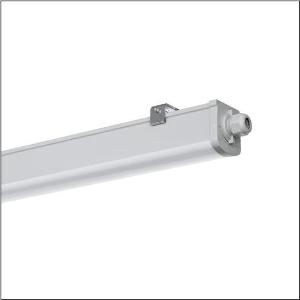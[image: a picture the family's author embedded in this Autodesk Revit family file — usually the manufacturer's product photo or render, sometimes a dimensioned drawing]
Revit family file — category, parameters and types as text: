
# Revit family: monsun_r__31_51fa207d420b_180d
name_source: partatom
category: Lighting Fixtures
units: mm (PartAtom-declared; Revit-internal decimal feet)

## family parameters
Cut with Voids When Loaded = No
Host = Face
Light Source = No
Part Type = Normal
Room Calculation Point = No
Round Connector Dimension = Use Diameter
Shared = No

## types (1)
- Monsun® 31 (1 x LED, 2300 lm, 19 W, 4000K)
    Apparent Load = 19 VA
    CIE Flux Codes = 42 72 91 92 100
    Color Rendering = 80
    Color Temperature = 4000K
    Default Elevation = 1800 mm
    Description = Monsun® 31, damp-proof luminaire, primary optical cover: diffuser, of PC, frosted, light emission: direct distribution, primary light characteristic: symmetric, installation type: surface-mounted, LED, rated luminous flux: 2.300lm, luminous efficacy: 121lm/W, light colour: 840, colour temperature: 4000K, control gear: ECG, with terminal, 3+1-pole, max. 2.5mm², through-wiring: 3x 2.5mm² + 1x 1.5mm², mains connection: 220..240V, AC, 50/60Hz, rated input power: 19W, housing, luminaire housing, of PC, light grey (RAL 7035), length: 558mm, width: 68mm, height: 76mm, protection rating (complete): IP66, insulation class (complete): insulation class II (safety insulation), certification: CE, ENEC, UKCA, protection symbol: D, impact resistance: IK08, permissible operating ambient temperature: -20..+40°C, corresponds to IFS (International Featured Standards) requirements for safety and quality in the food industry, contact your sales advisor before using the luminaires in applications with unclear chemical exposure, large temperature fluctuations or condensation-forming humidity, packaging unit: 1 piece
    Height = 77 mm
    Lamp = 1 x LED
    Lamp Light Flux = 2300 lm
    Lamp Power = 19 W
    Lamp count = 1
    Length = 618 mm
    Luminous efficacy = 121 lm/W
    Manufacturer = Siteco
    ModVariant = No
    Model = 51FA207D420B
    Mounting Place = Ceiling
    Mounting Type = Surface mounted
    Number of Poles = 1
    OnlyDefault = Yes
    Power Factor = 1
    Product Name = Monsun® 31
    Product group = damp-proof luminaire
    ProductGroupID = 301
    Protection Class = Protection class II
    Protection Degree = IP 66
    RLX_Detail_Level = 1
    RLX_Emergency_Light_Flux = 0 lm
    RLX_Emergency_Type = 0
    RLX_Emergency_Type_DB = No
    RlxData = <blob elided: 32893 chars, md5=0b5a2b5d>
    Socket = socket
    Standby Power = 0 W
    System Light Flux = 2300 lm
    System Power = 19 W
    Type Comments = Product without accessories
    Type Image = l_1006174.jpg
    URL = http://relux.com
    VarID = ---
    Voltage = 0 V
    Weight = 0.00 kg
    Width = 69 mm

## geometry (parser evidence)
native form markers: Blend x4, Sweep x13
no freeform markers — native parametric forms only
